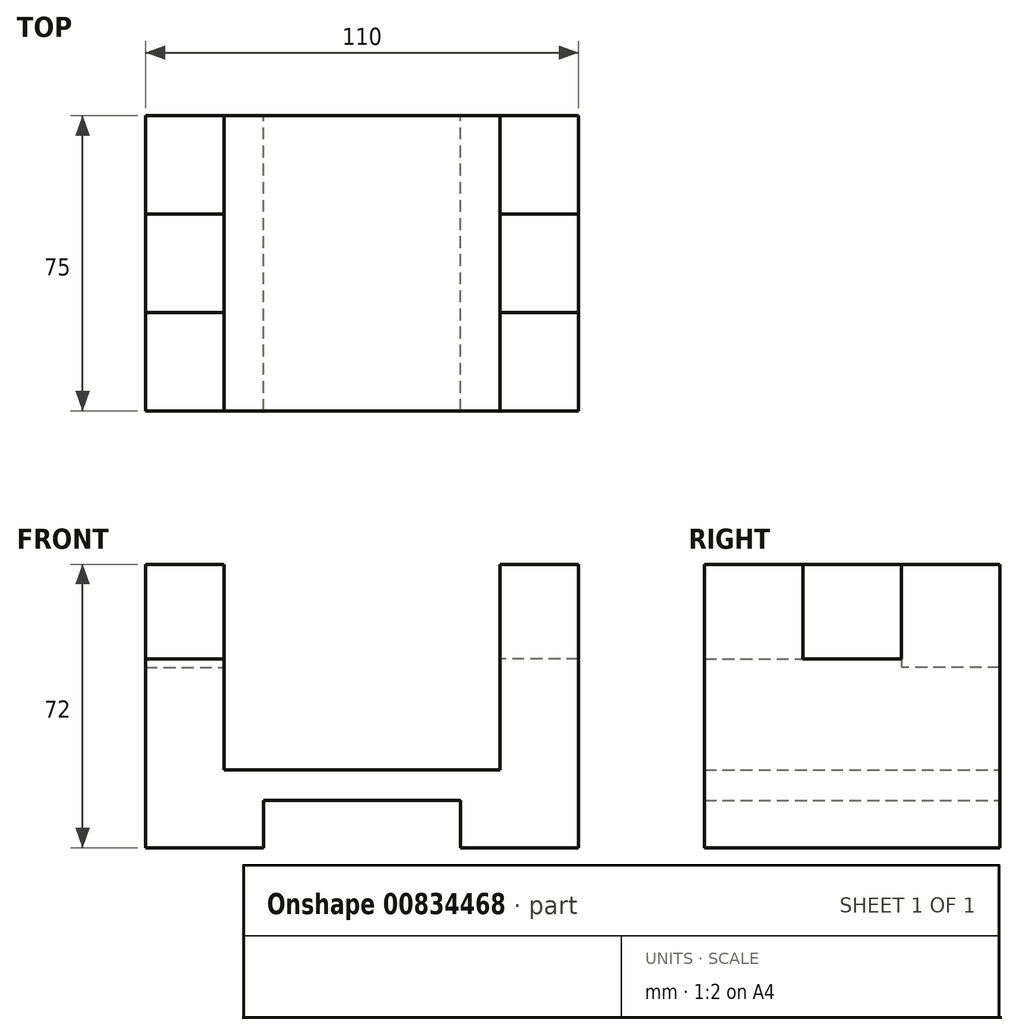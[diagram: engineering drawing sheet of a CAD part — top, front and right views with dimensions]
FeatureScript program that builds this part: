
annotation { "Feature Type Name" : "Feature", "Feature Type Description" : "" }
export const myFeature = defineFeature(function(context is Context, id is Id, definition is map)
    precondition{}
    {
        {
            var Q0;
            Q0=qCreatedBy(makeId("Front.planeOp"),FACE);
            var sketch = newSketch(context, id + "F0", { "sketchPlane" : qUnion([Q0])});
            skLineSegment(sketch, "E0", {"start": v(0, 0) * mm, "end": v(0, 72) * mm});
            skLineSegment(sketch, "E1", {"start": v(0, 72) * mm, "end": v(-20, 72) * mm});
            skLineSegment(sketch, "E2", {"start": v(-20, 72) * mm, "end": v(-20, 19.77) * mm});
            skLineSegment(sketch, "E3", {"start": v(-20, 19.77) * mm, "end": v(-90, 19.77) * mm});
            skLineSegment(sketch, "E4", {"start": v(-90, 19.77) * mm, "end": v(-90, 72) * mm});
            skLineSegment(sketch, "E5", {"start": v(-90, 72) * mm, "end": v(-110, 72) * mm});
            skLineSegment(sketch, "E6", {"start": v(-110, 72) * mm, "end": v(-110, 0) * mm});
            skLineSegment(sketch, "E7", {"start": v(-110, 0) * mm, "end": v(-80, 0) * mm});
            skLineSegment(sketch, "E8", {"start": v(-80, 0) * mm, "end": v(-80, 12) * mm});
            skLineSegment(sketch, "E9", {"start": v(-80, 12) * mm, "end": v(-30, 12) * mm});
            skLineSegment(sketch, "E10", {"start": v(-30, 12) * mm, "end": v(-30, 0) * mm});
            skLineSegment(sketch, "E11", {"start": v(-30, 0) * mm, "end": v(0, 0) * mm});
            skSolve(sketch);
        }
        {
            var Q0;
            Q0=makeQuery(id+"F0.imprint","IMPRINT",FACE,{"disambiguationData":[TD([[makeQuery(id+"F0.imprint","IMPRINT",EDGE,{"derivedFrom":sQuery(id+"F0.wireOp",EDGE,"E0")}),1.0]])]});
            extrude(context, id + "F1", {"entities" : qUnion([Q0]), "depth" : 75 * mm, "offsetDistance" : 25 * mm});
        }
        {
            var Q0;
            Q0=makeQuery(id+"F1.opExtrude","SWEPT_FACE",FACE,{"disambiguationData":[OSD([sQuery(id+"F0.wireOp",EDGE,"E4")])]});
            var sketch = newSketch(context, id + "F2", { "sketchPlane" : qUnion([Q0])});
            skLineSegment(sketch, "E12.bottom", {"start": v(-75, 72) * mm, "end": v(-50, 72) * mm});
            skLineSegment(sketch, "E12.top", {"start": v(-75, 48) * mm, "end": v(-50, 48) * mm});
            skLineSegment(sketch, "E12.left", {"start": v(-75, 72) * mm, "end": v(-75, 48) * mm});
            skLineSegment(sketch, "E12.right", {"start": v(-50, 72) * mm, "end": v(-50, 48) * mm});
            skPoint(sketch, "E13.oppositeSnap0", {"position": v(0, 45.89) * mm});
            skLineSegment(sketch, "E13.bottom", {"start": v(0, 72) * mm, "end": v(-25, 72) * mm});
            skLineSegment(sketch, "E13.top", {"start": v(0, 45.89) * mm, "end": v(-25, 45.89) * mm});
            skLineSegment(sketch, "E13.left", {"start": v(0, 72) * mm, "end": v(0, 45.89) * mm});
            skLineSegment(sketch, "E13.right", {"start": v(-25, 72) * mm, "end": v(-25, 45.89) * mm});
            skSolve(sketch);
        }
        {
            var Q0;
            Q0=makeQuery(id+"F2.imprint","IMPRINT",FACE,{"disambiguationData":[TD([[makeQuery(id+"F2.imprint","IMPRINT",EDGE,{"derivedFrom":sQuery(id+"F2.wireOp",EDGE,"E12.bottom")}),-1.0]])]});
            var Q1;
            Q1=makeQuery(id+"F2.imprint","IMPRINT",FACE,{"disambiguationData":[TD([[makeQuery(id+"F2.imprint","IMPRINT",EDGE,{"derivedFrom":sQuery(id+"F2.wireOp",EDGE,"E13.bottom")}),-1.0]])]});
            extrude(context, id + "F3", {"entities" : qUnion([Q0, Q1]), "operationType" : NewBodyOperationType.REMOVE, "oppositeDirection" : true, "depth" : 20 * mm, "offsetDistance" : 25 * mm});
        }
        {
            var Q0;
            Q0=makeQuery(id+"F1.opExtrude","SWEPT_FACE",FACE,{"disambiguationData":[OSD([sQuery(id+"F0.wireOp",EDGE,"E2")])]});
            var sketch = newSketch(context, id + "F4", { "sketchPlane" : qUnion([Q0])});
            skLineSegment(sketch, "E14.bottom", {"start": v(25, 72) * mm, "end": v(50, 72) * mm});
            skLineSegment(sketch, "E14.top", {"start": v(25, 48) * mm, "end": v(50, 48) * mm});
            skLineSegment(sketch, "E14.left", {"start": v(25, 72) * mm, "end": v(25, 48) * mm});
            skLineSegment(sketch, "E14.right", {"start": v(50, 72) * mm, "end": v(50, 48) * mm});
            skSolve(sketch);
        }
        {
            var Q0;
            Q0=makeQuery(id+"F4.imprint","IMPRINT",FACE,{"disambiguationData":[TD([[makeQuery(id+"F4.imprint","IMPRINT",EDGE,{"derivedFrom":sQuery(id+"F4.wireOp",EDGE,"E14.bottom")}),1.0]])]});
            extrude(context, id + "F5", {"entities" : qUnion([Q0]), "operationType" : NewBodyOperationType.REMOVE, "oppositeDirection" : true, "depth" : 20 * mm, "offsetDistance" : 25 * mm});
        }
    });
